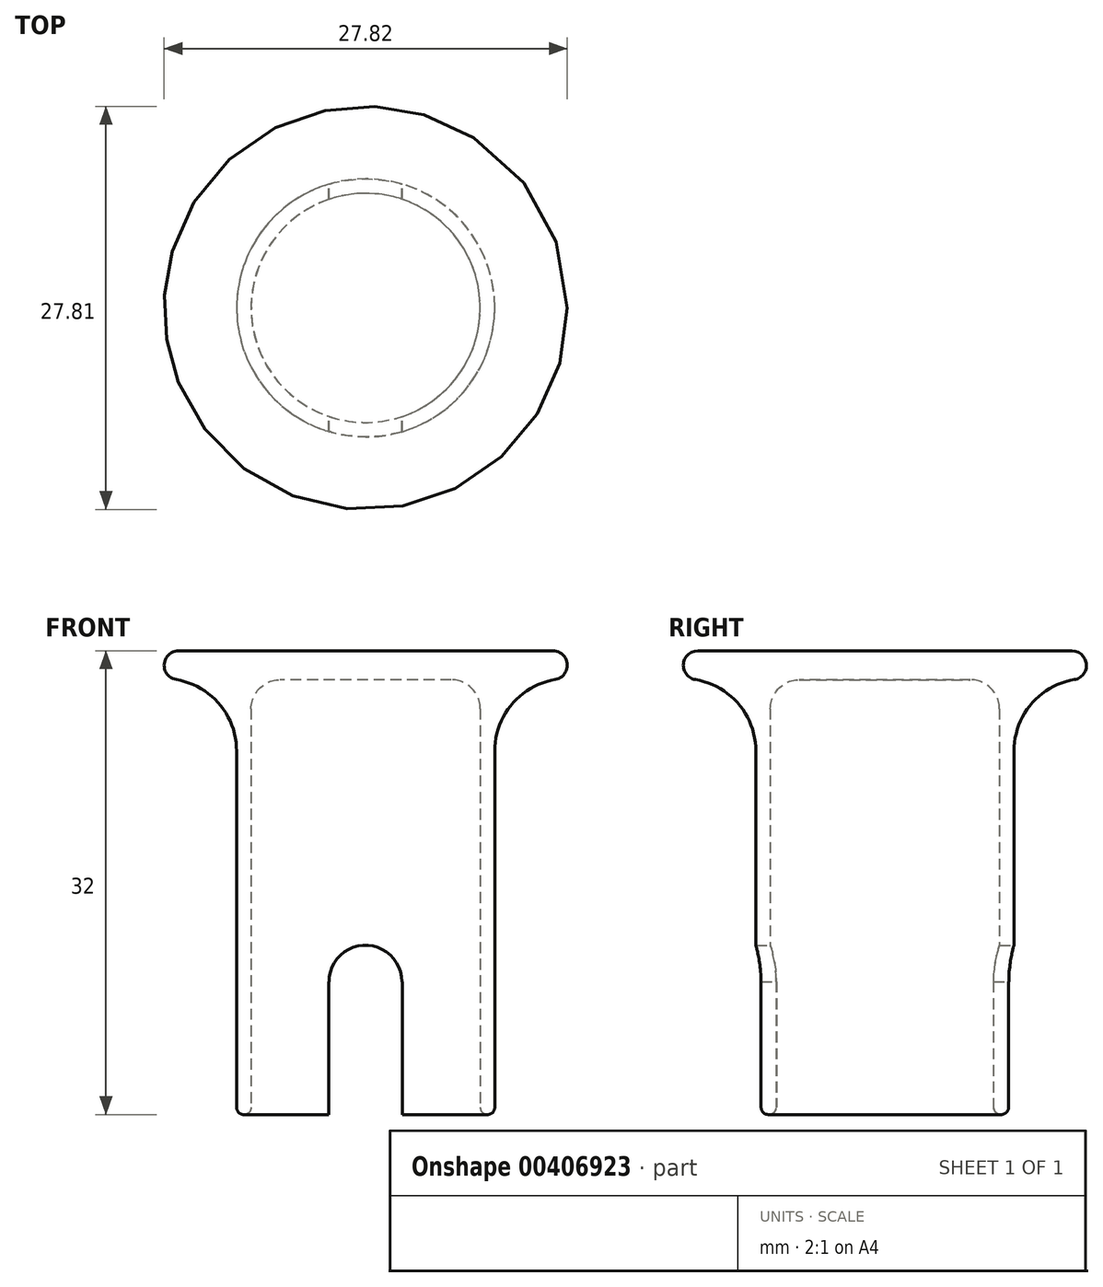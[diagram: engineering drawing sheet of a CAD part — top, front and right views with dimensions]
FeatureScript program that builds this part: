
annotation { "Feature Type Name" : "Feature", "Feature Type Description" : "" }
export const myFeature = defineFeature(function(context is Context, id is Id, definition is map)
    precondition{}
    {
        {
            var Q0;
            Q0=qCreatedBy(makeId("Right.planeOp"),FACE);
            var sketch = newSketch(context, id + "F0", { "sketchPlane" : qUnion([Q0])});
            skLineSegment(sketch, "E0", {"start": v(-34.6, -62.04) * mm, "end": v(-34.6, -32.04) * mm});
            skLineSegment(sketch, "E1", {"start": v(-34.6, -32.04) * mm, "end": v(-26.7, -32.04) * mm});
            skLineSegment(sketch, "E2", {"start": v(-26.7, -32.04) * mm, "end": v(-26.7, -30.04) * mm});
            skLineSegment(sketch, "E3", {"start": v(-26.7, -30.04) * mm, "end": v(-40.6, -30.04) * mm});
            skLineSegment(sketch, "E4", {"start": v(-40.6, -30.04) * mm, "end": v(-40.6, -32.04) * mm});
            skLineSegment(sketch, "E5", {"start": v(-40.6, -32.04) * mm, "end": v(-35.6, -32.04) * mm});
            skLineSegment(sketch, "E6", {"start": v(-35.6, -32.04) * mm, "end": v(-35.6, -62.04) * mm});
            skLineSegment(sketch, "E7", {"start": v(-35.6, -62.04) * mm, "end": v(-34.6, -62.04) * mm});
            skSolve(sketch);
        }
        {
            var Q0;
            Q0 = qSketchRegion(id + "F0", true);
            var Q1;
            Q1=sQuery(id+"F0.wireOp",EDGE,"E2");
            revolve(context, id + "F1", {"entities" : qUnion([Q0]), "axis" : qUnion([Q1]), "revolveType" : RevolveType.FULL});
        }
        {
            var Q0;
            Q0=makeQuery(id+"F1.opRevolve","SWEPT_EDGE",EDGE,{"disambiguationData":[OSD([sQuery(id+"F0.wireOp",EDGE,"E4"),sQuery(id+"F0.wireOp",EDGE,"E5")])]});
            var Q1;
            Q1=makeQuery(id+"F1.opRevolve","SWEPT_EDGE",EDGE,{"disambiguationData":[OSD([sQuery(id+"F0.wireOp",EDGE,"E3"),sQuery(id+"F0.wireOp",EDGE,"E4")])]});
            fillet(context, id + "F2", {"entities" : qUnion([Q0, Q1]), "radius" : 1 * mm, "tangentPropagation" : true, "allowEdgeOverflow" : false});
        }
        {
            var Q0;
            Q0=makeQuery(id+"F1.opRevolve","SWEPT_EDGE",EDGE,{"disambiguationData":[OSD([sQuery(id+"F0.wireOp",EDGE,"E5"),sQuery(id+"F0.wireOp",EDGE,"E6")])]});
            fillet(context, id + "F3", {"entities" : qUnion([Q0]), "radius" : 5 * mm, "tangentPropagation" : true, "allowEdgeOverflow" : false});
        }
        {
            var Q0;
            Q0=makeQuery(id+"F1.opRevolve","SWEPT_EDGE",EDGE,{"disambiguationData":[OSD([sQuery(id+"F0.wireOp",EDGE,"E0"),sQuery(id+"F0.wireOp",EDGE,"E7")])]});
            var Q1;
            Q1=makeQuery(id+"F1.opRevolve","SWEPT_EDGE",EDGE,{"disambiguationData":[OSD([sQuery(id+"F0.wireOp",EDGE,"E6"),sQuery(id+"F0.wireOp",EDGE,"E7")])]});
            fillet(context, id + "F4", {"entities" : qUnion([Q0, Q1]), "radius" : 0.5 * mm, "tangentPropagation" : true, "allowEdgeOverflow" : false});
        }
        {
            var Q0;
            Q0=qCreatedBy(makeId("Front.planeOp"),FACE);
            var sketch = newSketch(context, id + "F5", { "sketchPlane" : qUnion([Q0])});
            skCircle(sketch, "E8", {"center": v(0, -61.63) * mm, "radius": 2.42 * mm});
            skSolve(sketch);
        }
        {
            var Q0;
            Q0 = qSketchRegion(id + "F5", true);
            extrude(context, id + "F6", {"entities" : qUnion([Q0]), "operationType" : NewBodyOperationType.REMOVE, "depth" : 89.5 * mm});
        }
        {
            var Q0;
            Q0=makeQuery(id+"F1.opRevolve","SWEPT_EDGE",EDGE,{"disambiguationData":[OSD([sQuery(id+"F0.wireOp",EDGE,"E0"),sQuery(id+"F0.wireOp",EDGE,"E1")])]});
            fillet(context, id + "F7", {"entities" : qUnion([Q0]), "radius" : 2 * mm, "tangentPropagation" : true, "allowEdgeOverflow" : false});
        }
        {
            var Q0;
            Q0=qCreatedBy(makeId("Front.planeOp"),FACE);
            var sketch = newSketch(context, id + "F8", { "sketchPlane" : qUnion([Q0])});
            skLineSegment(sketch, "E9", {"start": v(-2.55, -62.08) * mm, "end": v(-2.55, -52.87) * mm});
            skLineSegment(sketch, "E10", {"start": v(2.52, -62.07) * mm, "end": v(2.52, -52.87) * mm});
            skLineSegment(sketch, "E11", {"start": v(2.52, -52.87) * mm, "end": v(-2.55, -52.87) * mm});
            skCircle(sketch, "E12", {"center": v(-0.02, -52.87) * mm, "radius": 2.51 * mm});
            skLineSegment(sketch, "E13", {"start": v(-2.55, -62.08) * mm, "end": v(2.52, -62.07) * mm});
            skSolve(sketch);
        }
        {
            var Q0;
            Q0 = qSketchRegion(id + "F8", true);
            extrude(context, id + "F9", {"entities" : qUnion([Q0]), "operationType" : NewBodyOperationType.REMOVE, "depth" : 39.1 * mm, "offsetDistance" : 25 * mm});
        }
    });
